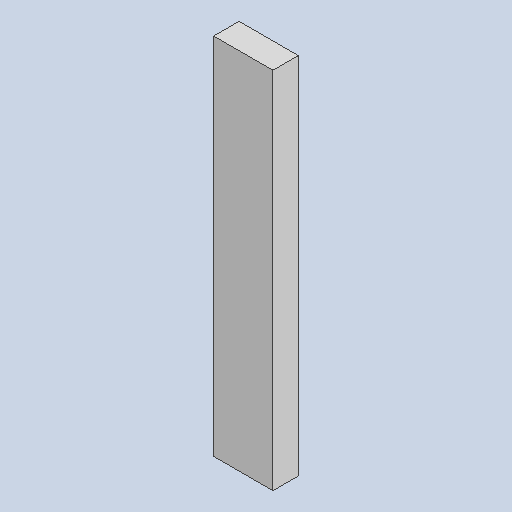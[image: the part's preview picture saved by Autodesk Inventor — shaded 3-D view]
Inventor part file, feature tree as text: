
AUTODESK INVENTOR PART (.ipt)
format: ipt  version: 2025 (Build 290162000, 162)  size: 79,872 bytes
history: native  units: in
note: dims shown in document units (in); Inventor stores cm internally (conversion verified against a paired STEP export)
features: other x3, sketch x1
ambient origin geometry x8: Origin, YZ Plane, XZ Plane, XY Plane, X Axis, Y Axis, Z Axis, Center Point
bodies: Solid1 (feature_tree)
feature tree (4):
  other  "side-slant.ipt"
  other  "Solid1::side-slant.ipt"
  other  "TaggingFeature1"
  sketch  "Sketch1"  dims[d0=0.3937in]
